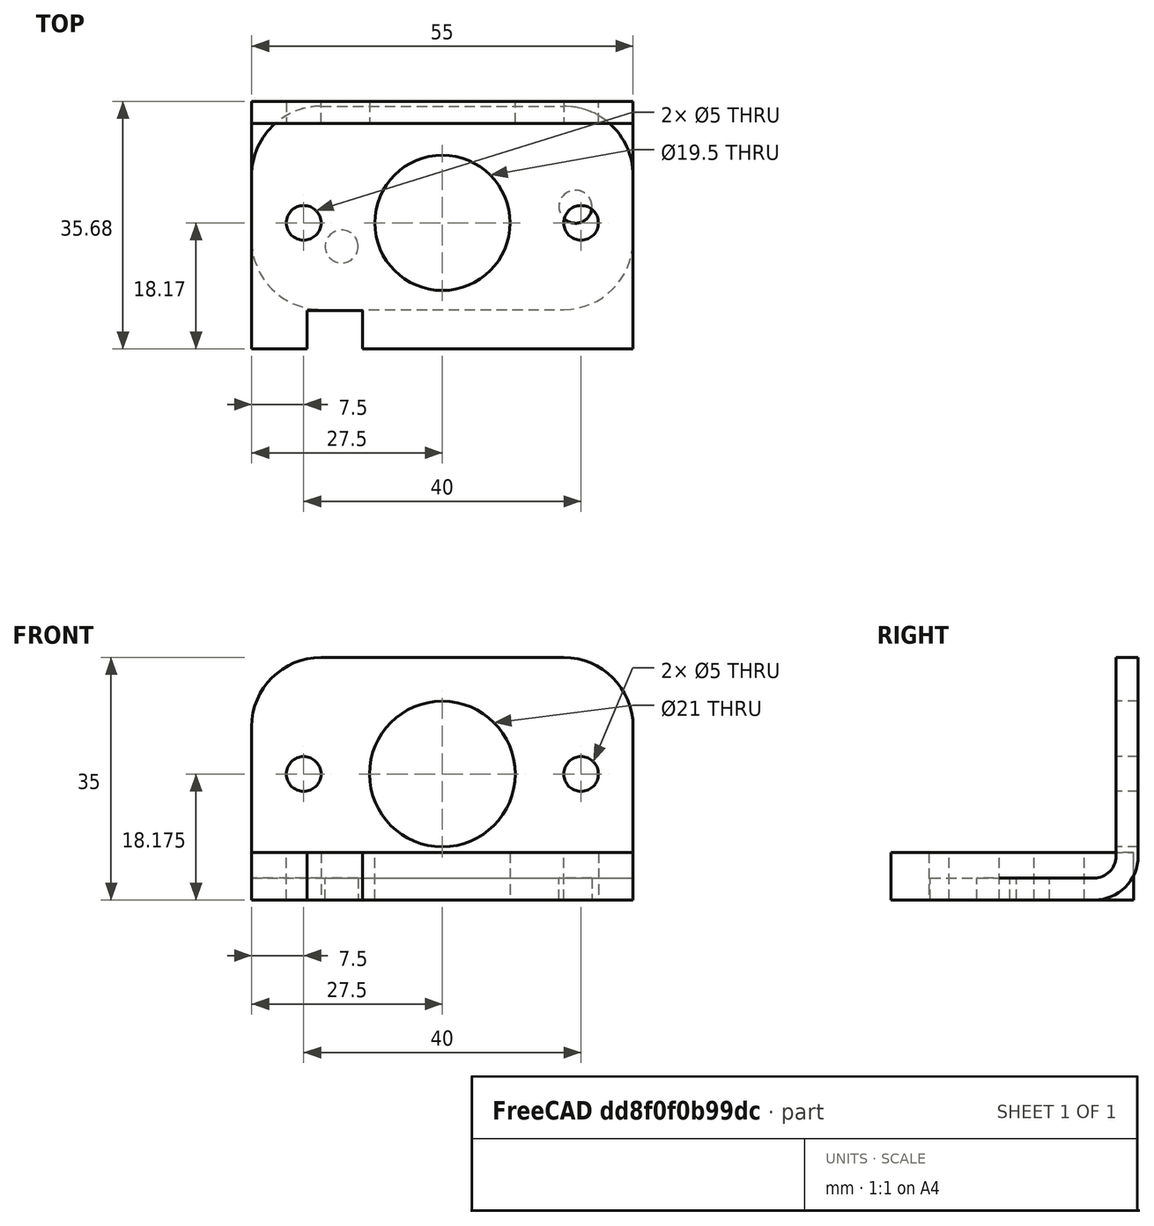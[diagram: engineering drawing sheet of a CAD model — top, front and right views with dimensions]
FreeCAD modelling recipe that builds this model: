
FCSTD DOCUMENT  (FreeCAD 1.0R39319 (Git))
Label: RudderPedalBracketAssembly
License: All rights reserved
LicenseURL: https://en.wikipedia.org/wiki/All_rights_reserved
objects: Sketcher::SketchObject×5, PartDesign::Pocket×5, App::Link×4, App::FeaturePython×4, PartDesign::FeaturePython×3, PartDesign::Fillet×3, PartDesign::Body×3, Assembly::JointGroup×1, Assembly::AssemblyObject×1
note: 43 computed .brp shape members not serialized (recipe doc carries the construction recipe); baked Part::Feature solids carry a one-line shape summary decoded from their .brp

FEATURE [PartDesign::FeaturePython] BaseShape  # WARN: FeaturePython — macro-defined, semantics opaque (R4)
  Suppressed = false
  fillGaps = true
  flangeWidth = 5
  height = 35
  length = 55
  originLoc = 4
  radius = 3.175
  shapeType = 1
  thickness = 3.175
  width = 30
FEATURE [Sketcher::SketchObject] Sketch001
  ArcFitTolerance = 1e-06
  FullyConstrained = true
  MakeInternals = false
  MapMode = 5
  Placement = pos=(0,15,0) rot=(1,0,0;1.5708rad)
  sketch-geometry (3):
    g0: Circle CenterX=0 CenterY=18.175 CenterZ=0 NormalX=0 NormalY=0 NormalZ=1 AngleXU=0 Radius=10.5
    g1: Circle CenterX=-20 CenterY=18.175 CenterZ=0 NormalX=0 NormalY=0 NormalZ=1 AngleXU=0 Radius=2.5
    g2: Circle CenterX=20 CenterY=18.175 CenterZ=0 NormalX=0 NormalY=0 NormalZ=1 AngleXU=0 Radius=2.5
  constraints (9):
    c: Diameter(g0) = 21
    c: PointOnObject(g0,g-2)
    c: DistanceY(g-3,g0) = 15
    c: Diameter(g1) = 5
    c: Diameter(g2) = 5
    c: Horizontal(g0,g2)
    c: Horizontal(g1,g0)
    c: DistanceX(g1,g0) = 20
    c: DistanceX(g0,g2) = 20
FEATURE [App::Link] Bracket  label="LeftBracket001"
  LinkedObject = -> Body
FEATURE [App::Link] Bearing  label="LeftBearing"
  LinkPlacement = pos=(9e-16,18.175,17.505) rot=(0,0.707107,0.707107;3.14159rad)
  LinkedObject = -> Body001
  Placement = pos=(9e-16,18.175,17.505) rot=(0,0.707107,0.707107;3.14159rad)
FEATURE [PartDesign::FeaturePython] BaseShape001  # WARN: FeaturePython — macro-defined, semantics opaque (R4)
  Suppressed = false
  fillGaps = true
  flangeWidth = 5
  height = 10
  length = 55
  originLoc = 4
  radius = 1
  shapeType = 0
  thickness = 6.858
  width = 35
FEATURE [Sketcher::SketchObject] Sketch002
  ArcFitTolerance = 1e-06
  AttachmentSupport = -> [BaseShape001]
  ExternalGeometry = -> [BaseShape001]
  FullyConstrained = true
  MakeInternals = false
  MapMode = 5
  Placement = pos=(0,0,6.858) rot=(0,0,1;0rad)
  sketch-geometry (7):
    g0: Circle CenterX=0 CenterY=0.67 CenterZ=0 NormalX=0 NormalY=0 NormalZ=1 AngleXU=0 Radius=9.75
    g1: Circle CenterX=-20 CenterY=0.67 CenterZ=0 NormalX=0 NormalY=0 NormalZ=1 AngleXU=0 Radius=2.5
    g2: Circle CenterX=20 CenterY=0.67 CenterZ=0 NormalX=0 NormalY=0 NormalZ=1 AngleXU=0 Radius=2.5
    g3: LineSegment StartX=-19.5 StartY=-17.5 StartZ=0 EndX=-11.5 EndY=-17.5 EndZ=0
    g4: LineSegment StartX=-11.5 StartY=-17.5 StartZ=0 EndX=-11.5 EndY=-12 EndZ=0
    g5: LineSegment StartX=-11.5 StartY=-12 StartZ=0 EndX=-19.5 EndY=-12 EndZ=0
    g6: LineSegment StartX=-19.5 StartY=-12 StartZ=0 EndX=-19.5 EndY=-17.5 EndZ=0
  constraints (21):
    c: Diameter(g0) = 19.5
    c: Diameter(g1) = 5
    c: Diameter(g2) = 5
    c: DistanceX(g1,g0) = 20
    c: DistanceX(g0,g2) = 20
    c: DistanceY(g-3,g0) = 18.17
    c: Vertical(g0,g-1)
    c: Horizontal(g1,g0)
    c: Horizontal(g2,g0)
    c: Coincident(g3,g4)
    c: Coincident(g4,g5)
    c: Coincident(g5,g6)
    c: Coincident(g6,g3)
    c: Horizontal(g3)
    c: Horizontal(g5)
    c: Vertical(g4)
    c: Vertical(g6)
    c: PointOnObject(g3,g-3)
    c: DistanceX(g-3,g3) = 8
    c: DistanceY(g3,g5) = 5.5
    c: DistanceX(g3,g3) = 8
FEATURE [PartDesign::Pocket] Pocket001
  BaseFeature = -> BaseShape001
  Direction = (0,0,-1)
  Length = 5
  Length2 = 5
  Profile = -> Sketch002
  ReferenceAxis = -> Sketch002 [N_Axis]
  Refine = true
  Suppressed = false
  Type = 1
FEATURE [App::FeaturePython] GroundedJoint  # Assembly grounded joint (typed FeaturePython)
  ObjectToGround = -> Bracket
FEATURE [PartDesign::FeaturePython] BaseShape002  # WARN: FeaturePython — macro-defined, semantics opaque (R4)
  Suppressed = false
  fillGaps = true
  flangeWidth = 5
  height = 35
  length = 55
  originLoc = 4
  radius = 3.175
  shapeType = 1
  thickness = 3.175
  width = 30
FEATURE [Sketcher::SketchObject] Sketch003
  ArcFitTolerance = 1e-06
  AttachmentSupport = -> [BaseShape002]
  ExternalGeometry = -> [BaseShape002]
  FullyConstrained = true
  MakeInternals = false
  MapMode = 5
  Placement = pos=(0,0,3.175) rot=(0,0,1;0rad)
  sketch-geometry (2):
    g0: Circle CenterX=-14.523 CenterY=-2.74 CenterZ=0 NormalX=0 NormalY=0 NormalZ=1 AngleXU=0 Radius=2.38125
    g1: Circle CenterX=19.186 CenterY=3 CenterZ=0 NormalX=0 NormalY=0 NormalZ=1 AngleXU=0 Radius=2.38125
  constraints (6):
    c: Diameter(g0) = 4.7625
    c: Diameter(g1) = 4.7625
    c: DistanceY(g1,g-3) = 12
    c: DistanceX(g0,g1) = 33.709
    c: DistanceX(g0,g-1) = 14.523
    c: DistanceY(g0,g1) = 5.74
FEATURE [PartDesign::Pocket] Pocket002  label="PocketBase001"
  BaseFeature = -> BaseShape002
  Direction = (0,0,-1)
  Length = 5
  Length2 = 5
  Profile = -> Sketch003
  ReferenceAxis = -> Sketch003 [N_Axis]
  Refine = true
  Suppressed = false
  Type = 1
FEATURE [Sketcher::SketchObject] Sketch004
  ArcFitTolerance = 1e-06
  AttachmentSupport = -> [Pocket002]
  ExternalGeometry = -> [Pocket002]
  FullyConstrained = true
  MakeInternals = false
  MapMode = 5
  Placement = pos=(0,15,0) rot=(1,0,0;1.5708rad)
  sketch-geometry (3):
    g0: Circle CenterX=0 CenterY=18.175 CenterZ=0 NormalX=0 NormalY=0 NormalZ=1 AngleXU=0 Radius=10.5
    g1: Circle CenterX=-20 CenterY=18.175 CenterZ=0 NormalX=0 NormalY=0 NormalZ=1 AngleXU=0 Radius=2.5
    g2: Circle CenterX=20 CenterY=18.175 CenterZ=0 NormalX=0 NormalY=0 NormalZ=1 AngleXU=0 Radius=2.5
  constraints (9):
    c: Diameter(g0) = 21
    c: Diameter(g1) = 5
    c: Diameter(g2) = 5
    c: Horizontal(g1,g0)
    c: Horizontal(g0,g2)
    c: DistanceX(g1,g0) = 20
    c: DistanceX(g0,g2) = 20
    c: DistanceY(g-3,g0) = 15
    c: Vertical(g0,g-1)
FEATURE [App::Link] RightBracket  label="RightBracket001"
  LinkPlacement = pos=(-6.39716e-06,76.35,1.90735e-06) rot=(0,0,1;3.14159rad)
  LinkedObject = -> Body002
  Placement = pos=(-6.39716e-06,76.35,1.90735e-06) rot=(0,0,1;3.14159rad)
FEATURE [PartDesign::Pocket] Pocket003  label="PocketUpper001"
  BaseFeature = -> Pocket002
  Direction = (0,1,-2e-16)
  Length = 5
  Length2 = 5
  Profile = -> Sketch004
  ReferenceAxis = -> Sketch004 [N_Axis]
  Refine = true
  Suppressed = false
  Type = 1
FEATURE [App::Link] Bearing001  label="RightBearing"
  LinkPlacement = pos=(-4.20871e-06,51.317,17.505) rot=(0,0.707107,0.707107;3.14159rad)
  LinkedObject = -> Body001
  Placement = pos=(-4.20871e-06,51.317,17.505) rot=(0,0.707107,0.707107;3.14159rad)
FEATURE [App::FeaturePython] GroundedJoint001  # Assembly grounded joint (typed FeaturePython)
  ObjectToGround = -> RightBracket
  Placement = pos=(-6.39716e-06,76.35,1.90735e-06) rot=(0,0,1;3.14159rad)
FEATURE [PartDesign::Fillet] Fillet001
  Base = -> Pocket003 [Edge22,Edge12,Edge2,Edge4]
  BaseFeature = -> Pocket003
  Radius = 10
  Refine = true
  SupportTransform = false
  Suppressed = false
  UseAllEdges = false
FEATURE [PartDesign::Body] Body002  label="RightBracket"
  AllowCompound = false
  Group = -> [BaseShape002,Sketch003,Pocket002,Sketch004,Pocket003,Fillet001]
  Origin = -> Origin003
  Tip = -> Fillet001
FEATURE [PartDesign::Fillet] Fillet002
  Base = -> Pocket001 [Edge3,Edge18]
  BaseFeature = -> Pocket001
  Radius = 10
  Refine = true
  SupportTransform = false
  Suppressed = false
  UseAllEdges = false
FEATURE [PartDesign::Body] Body001  label="Bearing"
  AllowCompound = false
  Group = -> [BaseShape001,Sketch002,Pocket001,Fillet002]
  Origin = -> Origin002
  Tip = -> Fillet002
FEATURE [Sketcher::SketchObject] Sketch
  ArcFitTolerance = 1e-06
  AttachmentSupport = -> [BaseShape]
  ExternalGeometry = -> [BaseShape]
  FullyConstrained = true
  MakeInternals = false
  MapMode = 5
  Placement = pos=(0,0,3.175) rot=(0,0,1;0rad)
  sketch-geometry (2):
    g0: Circle CenterX=-17.437 CenterY=3 CenterZ=0 NormalX=0 NormalY=0 NormalZ=1 AngleXU=0 Radius=2.3815
    g1: Circle CenterX=16.272 CenterY=-2.735 CenterZ=0 NormalX=0 NormalY=0 NormalZ=1 AngleXU=0 Radius=2.3815
  constraints (6):
    c: Diameter(g0) = 4.763
    c: Diameter(g1) = 4.763
    c: DistanceX(g0,g1) = 33.709
    c: DistanceY(g1,g0) = 5.735
    c: DistanceX(g0,g-1) = 17.437
    c: DistanceY(g0,g-3) = 12
FEATURE [PartDesign::Pocket] Pocket004  label="PocketBase"
  BaseFeature = -> BaseShape
  Direction = (0,0,-1)
  Length = 5
  Length2 = 5
  Profile = -> Sketch
  ReferenceAxis = -> Sketch [N_Axis]
  Refine = true
  Suppressed = false
  Type = 1
FEATURE [PartDesign::Pocket] Pocket  label="PocketUpper"
  BaseFeature = -> Pocket004
  Direction = (0,1,-2e-16)
  Length = 5
  Length2 = 5
  Profile = -> Sketch001
  ReferenceAxis = -> Sketch001 [N_Axis]
  Refine = true
  Suppressed = false
  Type = 1
FEATURE [PartDesign::Fillet] Fillet
  Base = -> Pocket [Edge22,Edge12,Edge2,Edge4]
  BaseFeature = -> Pocket
  Radius = 10
  Refine = true
  SupportTransform = false
  Suppressed = false
  UseAllEdges = false
FEATURE [PartDesign::Body] Body  label="LeftBracket"
  AllowCompound = false
  Group = -> [BaseShape,Pocket004,Sketch,Sketch001,Pocket,Fillet]
  Origin = -> Origin
  Tip = -> Fillet
FEATURE [App::FeaturePython] Joint  label="Fixed"  # Assembly joint (typed FeaturePython)
  Activated = true
  AngleMax = 0
  AngleMin = 0
  Detach1 = false
  Detach2 = false
  Distance = 0
  Distance2 = 0
  EnableAngleMax = false
  EnableAngleMin = false
  EnableLengthMax = false
  EnableLengthMin = false
  JointType = 0 (Fixed)
  LengthMax = 0
  LengthMin = 0
  Placement1 = pos=(-20,0.67,0) rot=(0,0,1;0rad)
  Placement2 = pos=(20,18.175,18.175) rot=(0,0.707107,0.707107;3.14159rad)
  Reference1 = -> Assembly [Bearing.Face5,Bearing.Edge11]
  Reference2 = -> Assembly [Bracket.Face14,Bracket.Edge7]
FEATURE [App::FeaturePython] Joint001  label="Fixed001"  # Assembly joint (typed FeaturePython)
  Activated = true
  AngleMax = 0
  AngleMin = 0
  Detach1 = false
  Detach2 = false
  Distance = 0
  Distance2 = 0
  EnableAngleMax = false
  EnableAngleMin = false
  EnableLengthMax = false
  EnableLengthMin = false
  JointType = 0 (Fixed)
  LengthMax = 0
  LengthMin = 0
  Placement1 = pos=(-20,0.67,6.858) rot=(0,0,1;0rad)
  Placement2 = pos=(-20,18.175,18.175) rot=(1,0,0;1.5708rad)
  Reference1 = -> Assembly [Bearing001.Edge14,Bearing001.Edge14]
  Reference2 = -> Assembly [RightBracket.Edge47,RightBracket.Edge47]
FEATURE [Assembly::JointGroup] Joints
  Group = -> [GroundedJoint,GroundedJoint001,Joint,Joint001]
FEATURE [Assembly::AssemblyObject] Assembly
  Group = -> [Joints,Bracket,Bearing,GroundedJoint,RightBracket,Bearing001,GroundedJoint001,Joint,Joint001]
  Origin = -> Origin001
  Placement = pos=(0,0,0) rot=(0,0,1;3.14159rad)
  Type = Assembly
